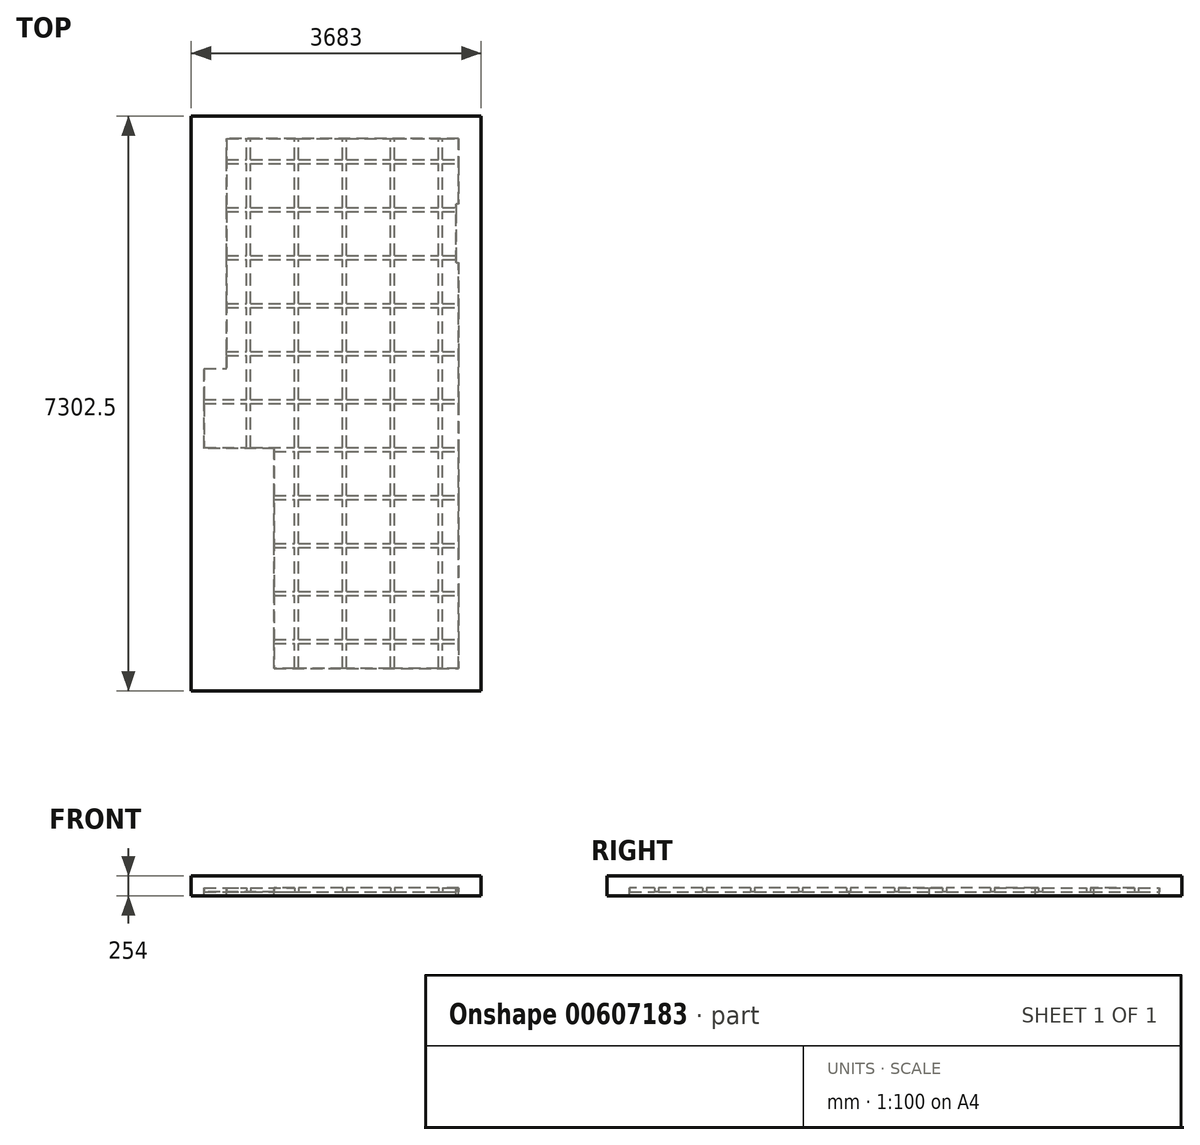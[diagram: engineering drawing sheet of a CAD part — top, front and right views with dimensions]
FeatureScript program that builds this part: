
annotation { "Feature Type Name" : "Feature", "Feature Type Description" : "" }
export const myFeature = defineFeature(function(context is Context, id is Id, definition is map)
    precondition{}
    {
        {
            var Q0;
            Q0=qCreatedBy(makeId("Top.planeOp"),FACE);
            var sketch = newSketch(context, id + "F0", { "sketchPlane" : qUnion([Q0])});
            skLineSegment(sketch, "E0", {"start": v(0, 0) * mm, "end": v(0, 5156.2) * mm});
            skLineSegment(sketch, "E1", {"start": v(0, 5156.2) * mm, "end": v(-34.92, 5156.2) * mm});
            skLineSegment(sketch, "E2", {"start": v(-34.92, 5156.2) * mm, "end": v(-34.92, 5899.15) * mm});
            skLineSegment(sketch, "E3", {"start": v(-34.92, 5899.15) * mm, "end": v(0, 5899.15) * mm});
            skLineSegment(sketch, "E4", {"start": v(0, 5899.15) * mm, "end": v(0, 6731) * mm});
            skLineSegment(sketch, "E5", {"start": v(0, 6731) * mm, "end": v(-2946.4, 6731) * mm});
            skLineSegment(sketch, "E6", {"start": v(-2946.4, 6731) * mm, "end": v(-2946.4, 3810) * mm});
            skLineSegment(sketch, "E7", {"start": v(-2946.4, 3810) * mm, "end": v(-3232.15, 3810) * mm});
            skLineSegment(sketch, "E8", {"start": v(-3232.15, 3810) * mm, "end": v(-3232.15, 2794) * mm});
            skLineSegment(sketch, "E9", {"start": v(-3232.15, 2794) * mm, "end": v(-2343.15, 2794) * mm});
            skLineSegment(sketch, "E10", {"start": v(-2343.15, 2794) * mm, "end": v(-2343.15, 0) * mm});
            skLineSegment(sketch, "E11", {"start": v(-2343.15, 0) * mm, "end": v(0, 0) * mm});
            skLineSegment(sketch, "E12", {"start": v(285.75, 7016.75) * mm, "end": v(285.75, -285.75) * mm});
            skLineSegment(sketch, "E13", {"start": v(285.75, -285.75) * mm, "end": v(-3397.25, -285.75) * mm});
            skLineSegment(sketch, "E14", {"start": v(285.75, 7016.75) * mm, "end": v(-3397.25, 7016.75) * mm});
            skLineSegment(sketch, "E15", {"start": v(-3397.25, 7016.75) * mm, "end": v(-3397.25, -285.75) * mm});
            skSolve(sketch);
        }
        {
            var Q0;
            Q0=makeQuery(id+"F0.imprint","IMPRINT",FACE,{"disambiguationData":[TD([[makeQuery(id+"F0.imprint","IMPRINT",EDGE,{"derivedFrom":sQuery(id+"F0.wireOp",EDGE,"E0")}),-1.0]])]});
            extrude(context, id + "F1", {"entities" : qUnion([Q0]), "oppositeDirection" : true, "depth" : 254 * mm, "offsetDistance" : 25.4 * mm});
        }
        {
            var Q0;
            Q0=qSketchRegion(id+"F0",true);
            var Q1;
            Q1=makeQuery(id+"F0.imprint","IMPRINT",FACE,{"disambiguationData":[TD([[makeQuery(id+"F0.imprint","IMPRINT",EDGE,{"derivedFrom":sQuery(id+"F0.wireOp",EDGE,"E0")}),1.0]])]});
            extrude(context, id + "F2", {"entities" : qUnion([Q0, Q1]), "operationType" : NewBodyOperationType.ADD, "oppositeDirection" : true, "depth" : 203.2 * mm, "offsetDistance" : 25.4 * mm});
        }
        {
            var Q0;
            Q0=makeQuery(id+"F2.opExtrude","CAP_FACE",FACE,{"disambiguationData":[OSD([sQuery(id+"F0.wireOp",EDGE,"E12"),sQuery(id+"F0.wireOp",EDGE,"E13"),sQuery(id+"F0.wireOp",EDGE,"E14"),sQuery(id+"F0.wireOp",EDGE,"E15")])],"isStart":false});
            var sketch = newSketch(context, id + "F3", { "sketchPlane" : qUnion([Q0])});
            skLineSegment(sketch, "E16.bottom", {"start": v(-2035.18, 0) * mm, "end": v(-2085.98, 0) * mm});
            skLineSegment(sketch, "E16.top", {"start": v(-2035.18, -6731) * mm, "end": v(-2085.98, -6731) * mm});
            skLineSegment(sketch, "E16.left", {"start": v(-2035.18, 0) * mm, "end": v(-2035.18, -317.5) * mm});
            skLineSegment(sketch, "E16.right", {"start": v(-2085.98, 0) * mm, "end": v(-2085.98, -317.5) * mm});
            skLineSegment(sketch, "E17.bottom", {"start": v(-1425.58, 0) * mm, "end": v(-1476.38, 0) * mm});
            skLineSegment(sketch, "E17.top", {"start": v(-1425.58, -6731) * mm, "end": v(-1476.38, -6731) * mm});
            skLineSegment(sketch, "E17.left", {"start": v(-1425.58, 0) * mm, "end": v(-1425.58, -317.5) * mm});
            skLineSegment(sketch, "E17.right", {"start": v(-1476.38, 0) * mm, "end": v(-1476.38, -317.5) * mm});
            skPoint(sketch, "E18.oppositeSnap0", {"position": v(-866.78, 0) * mm});
            skLineSegment(sketch, "E18.bottom", {"start": v(-815.98, 0) * mm, "end": v(-866.78, 0) * mm});
            skLineSegment(sketch, "E18.top", {"start": v(-815.98, -6731) * mm, "end": v(-866.78, -6731) * mm});
            skLineSegment(sketch, "E18.left", {"start": v(-815.98, 0) * mm, "end": v(-815.98, -317.5) * mm});
            skLineSegment(sketch, "E18.right", {"start": v(-866.78, 0) * mm, "end": v(-866.78, -317.5) * mm});
            skLineSegment(sketch, "E19.bottom", {"start": v(-257.18, 0) * mm, "end": v(-206.38, 0) * mm});
            skLineSegment(sketch, "E19.top", {"start": v(-257.18, -6731) * mm, "end": v(-206.38, -6731) * mm});
            skLineSegment(sketch, "E19.left", {"start": v(-257.18, 0) * mm, "end": v(-257.18, -317.5) * mm});
            skLineSegment(sketch, "E19.right", {"start": v(-206.38, 0) * mm, "end": v(-206.38, -317.5) * mm});
            skLineSegment(sketch, "E20.bottom", {"start": v(-2695.58, -2794) * mm, "end": v(-2644.78, -2794) * mm});
            skLineSegment(sketch, "E20.top", {"start": v(-2695.58, -6731) * mm, "end": v(-2644.78, -6731) * mm});
            skLineSegment(sketch, "E20.left", {"start": v(-2695.58, -2794) * mm, "end": v(-2695.58, -3365.5) * mm});
            skLineSegment(sketch, "E20.right", {"start": v(-2644.78, -2794) * mm, "end": v(-2644.78, -3365.5) * mm});
            skLineSegment(sketch, "E21.bottom", {"start": v(-2946.4, -6413.5) * mm, "end": v(-2695.58, -6413.5) * mm});
            skLineSegment(sketch, "E21.top", {"start": v(-2946.4, -6464.3) * mm, "end": v(-2695.58, -6464.3) * mm});
            skLineSegment(sketch, "E21.left", {"start": v(-2946.4, -6413.5) * mm, "end": v(-2946.4, -6464.3) * mm});
            skLineSegment(sketch, "E21.right", {"start": v(0, -6413.5) * mm, "end": v(0, -6464.3) * mm});
            skLineSegment(sketch, "E22.bottom", {"start": v(-2946.4, -5854.7) * mm, "end": v(-2695.58, -5854.7) * mm});
            skLineSegment(sketch, "E22.top", {"start": v(-2946.4, -5803.9) * mm, "end": v(-2695.58, -5803.9) * mm});
            skLineSegment(sketch, "E22.left", {"start": v(-2946.4, -5854.7) * mm, "end": v(-2946.4, -5803.9) * mm});
            skLineSegment(sketch, "E22.right", {"start": v(-34.92, -5854.7) * mm, "end": v(-34.92, -5803.9) * mm});
            skLineSegment(sketch, "E23.bottom", {"start": v(-2946.4, -5245.1) * mm, "end": v(-2695.58, -5245.1) * mm});
            skLineSegment(sketch, "E23.top", {"start": v(-2946.4, -5194.3) * mm, "end": v(-2695.58, -5194.3) * mm});
            skLineSegment(sketch, "E23.left", {"start": v(-2946.4, -5245.1) * mm, "end": v(-2946.4, -5194.3) * mm});
            skLineSegment(sketch, "E23.right", {"start": v(0, -5245.1) * mm, "end": v(0, -5194.3) * mm});
            skLineSegment(sketch, "E24.bottom", {"start": v(-2946.4, -4584.7) * mm, "end": v(-2695.58, -4584.7) * mm});
            skLineSegment(sketch, "E24.top", {"start": v(-2946.4, -4635.5) * mm, "end": v(-2695.58, -4635.5) * mm});
            skLineSegment(sketch, "E24.left", {"start": v(-2946.4, -4584.7) * mm, "end": v(-2946.4, -4635.5) * mm});
            skLineSegment(sketch, "E24.right", {"start": v(0, -4584.7) * mm, "end": v(0, -4635.5) * mm});
            skLineSegment(sketch, "E25.bottom", {"start": v(-2946.4, -3975.1) * mm, "end": v(-2695.58, -3975.1) * mm});
            skLineSegment(sketch, "E25.top", {"start": v(-2946.4, -4025.9) * mm, "end": v(-2695.58, -4025.9) * mm});
            skLineSegment(sketch, "E25.left", {"start": v(-2946.4, -3975.1) * mm, "end": v(-2946.4, -4025.9) * mm});
            skLineSegment(sketch, "E25.right", {"start": v(0, -3975.1) * mm, "end": v(0, -4025.9) * mm});
            skLineSegment(sketch, "E26.bottom", {"start": v(-3232.15, -3365.5) * mm, "end": v(-2695.58, -3365.5) * mm});
            skLineSegment(sketch, "E26.top", {"start": v(-3232.15, -3416.3) * mm, "end": v(-2695.58, -3416.3) * mm});
            skLineSegment(sketch, "E26.left", {"start": v(-3232.15, -3365.5) * mm, "end": v(-3232.15, -3416.3) * mm});
            skLineSegment(sketch, "E26.right", {"start": v(0, -3365.5) * mm, "end": v(0, -3416.3) * mm});
            skLineSegment(sketch, "E27.bottom", {"start": v(-3232.15, -2755.9) * mm, "end": v(-2085.98, -2755.9) * mm});
            skLineSegment(sketch, "E27.top", {"start": v(-3232.15, -2806.7) * mm, "end": v(-2695.58, -2806.7) * mm});
            skLineSegment(sketch, "E27.left", {"start": v(-3232.15, -2755.9) * mm, "end": v(-3232.15, -2806.7) * mm});
            skLineSegment(sketch, "E27.right", {"start": v(0, -2755.9) * mm, "end": v(0, -2806.7) * mm});
            skLineSegment(sketch, "E28.bottom", {"start": v(-2343.15, -2146.3) * mm, "end": v(-2085.98, -2146.3) * mm});
            skLineSegment(sketch, "E28.top", {"start": v(-2343.15, -2197.1) * mm, "end": v(-2085.98, -2197.1) * mm});
            skLineSegment(sketch, "E28.left", {"start": v(-2343.15, -2146.3) * mm, "end": v(-2343.15, -2197.1) * mm});
            skLineSegment(sketch, "E28.right", {"start": v(0, -2146.3) * mm, "end": v(0, -2197.1) * mm});
            skLineSegment(sketch, "E29.bottom", {"start": v(-2343.15, -1536.7) * mm, "end": v(-2085.98, -1536.7) * mm});
            skLineSegment(sketch, "E29.top", {"start": v(-2343.15, -1587.5) * mm, "end": v(-2085.98, -1587.5) * mm});
            skLineSegment(sketch, "E29.left", {"start": v(-2343.15, -1536.7) * mm, "end": v(-2343.15, -1587.5) * mm});
            skLineSegment(sketch, "E29.right", {"start": v(0, -1536.7) * mm, "end": v(0, -1587.5) * mm});
            skLineSegment(sketch, "E30.bottom", {"start": v(-2343.15, -927.1) * mm, "end": v(-2085.98, -927.1) * mm});
            skLineSegment(sketch, "E30.top", {"start": v(-2343.15, -977.9) * mm, "end": v(-2085.98, -977.9) * mm});
            skLineSegment(sketch, "E30.left", {"start": v(-2343.15, -927.1) * mm, "end": v(-2343.15, -977.9) * mm});
            skLineSegment(sketch, "E30.right", {"start": v(0, -927.1) * mm, "end": v(0, -977.9) * mm});
            skLineSegment(sketch, "E31.bottom", {"start": v(-2343.15, -317.5) * mm, "end": v(-2085.98, -317.5) * mm});
            skLineSegment(sketch, "E31.top", {"start": v(-2343.15, -368.3) * mm, "end": v(-2085.98, -368.3) * mm});
            skLineSegment(sketch, "E31.left", {"start": v(-2343.15, -317.5) * mm, "end": v(-2343.15, -368.3) * mm});
            skLineSegment(sketch, "E31.right", {"start": v(0, -317.5) * mm, "end": v(0, -368.3) * mm});
            skLineSegment(sketch, "E32.trimOffspring", {"start": v(-2085.98, -2806.7) * mm, "end": v(-2085.98, -3365.5) * mm});
            skLineSegment(sketch, "E33.trimOffspring", {"start": v(-2035.18, -2806.7) * mm, "end": v(-2035.18, -3365.5) * mm});
            skLineSegment(sketch, "E34.trimOffspring", {"start": v(-2035.18, -2755.9) * mm, "end": v(-1476.38, -2755.9) * mm});
            skLineSegment(sketch, "E35.trimOffspring", {"start": v(-1476.38, -2806.7) * mm, "end": v(-1476.38, -3365.5) * mm});
            skLineSegment(sketch, "E36.trimOffspring", {"start": v(-1425.58, -2755.9) * mm, "end": v(0, -2755.9) * mm});
            skLineSegment(sketch, "E37.trimOffspring", {"start": v(-1425.58, -2806.7) * mm, "end": v(-1425.58, -3365.5) * mm});
            skLineSegment(sketch, "E38.trimOffspring", {"start": v(-1425.58, -2806.7) * mm, "end": v(0, -2806.7) * mm});
            skLineSegment(sketch, "E39.trimOffspring", {"start": v(-2035.18, -317.5) * mm, "end": v(-1476.38, -317.5) * mm});
            skLineSegment(sketch, "E40.trimOffspring", {"start": v(-2085.98, -368.3) * mm, "end": v(-2085.98, -927.1) * mm});
            skLineSegment(sketch, "E41.trimOffspring", {"start": v(-2035.18, -368.3) * mm, "end": v(-2035.18, -927.1) * mm});
            skLineSegment(sketch, "E42.trimOffspring", {"start": v(-2035.18, -368.3) * mm, "end": v(-1476.38, -368.3) * mm});
            skLineSegment(sketch, "E43.trimOffspring", {"start": v(-1476.38, -368.3) * mm, "end": v(-1476.38, -927.1) * mm});
            skLineSegment(sketch, "E44.trimOffspring", {"start": v(-1425.58, -317.5) * mm, "end": v(-866.78, -317.5) * mm});
            skLineSegment(sketch, "E45.trimOffspring", {"start": v(-1425.58, -368.3) * mm, "end": v(-1425.58, -927.1) * mm});
            skLineSegment(sketch, "E46.trimOffspring", {"start": v(-1425.58, -368.3) * mm, "end": v(-866.78, -368.3) * mm});
            skLineSegment(sketch, "E47.trimOffspring", {"start": v(-866.78, -368.3) * mm, "end": v(-866.78, -927.1) * mm});
            skLineSegment(sketch, "E48.trimOffspring", {"start": v(-815.98, -317.5) * mm, "end": v(-257.18, -317.5) * mm});
            skLineSegment(sketch, "E49.trimOffspring", {"start": v(-815.98, -368.3) * mm, "end": v(-257.18, -368.3) * mm});
            skLineSegment(sketch, "E50.trimOffspring", {"start": v(-815.98, -368.3) * mm, "end": v(-815.98, -927.1) * mm});
            skLineSegment(sketch, "E51.trimOffspring", {"start": v(-257.18, -368.3) * mm, "end": v(-257.18, -927.1) * mm});
            skLineSegment(sketch, "E52.trimOffspring", {"start": v(-206.37, -317.5) * mm, "end": v(0, -317.5) * mm});
            skLineSegment(sketch, "E53.trimOffspring", {"start": v(-206.38, -368.3) * mm, "end": v(-206.38, -927.1) * mm});
            skLineSegment(sketch, "E54.trimOffspring", {"start": v(-206.37, -368.3) * mm, "end": v(0, -368.3) * mm});
            skLineSegment(sketch, "E55.trimOffspring", {"start": v(-206.37, -927.1) * mm, "end": v(0, -927.1) * mm});
            skLineSegment(sketch, "E56.trimOffspring", {"start": v(-206.37, -977.9) * mm, "end": v(0, -977.9) * mm});
            skLineSegment(sketch, "E57.trimOffspring", {"start": v(-206.38, -977.9) * mm, "end": v(-206.38, -1536.7) * mm});
            skLineSegment(sketch, "E58.trimOffspring", {"start": v(-257.18, -977.9) * mm, "end": v(-257.18, -1536.7) * mm});
            skLineSegment(sketch, "E59.trimOffspring", {"start": v(-815.98, -977.9) * mm, "end": v(-815.98, -1536.7) * mm});
            skLineSegment(sketch, "E60.trimOffspring", {"start": v(-866.78, -977.9) * mm, "end": v(-866.78, -1536.7) * mm});
            skLineSegment(sketch, "E61.trimOffspring", {"start": v(-815.98, -927.1) * mm, "end": v(-257.18, -927.1) * mm});
            skLineSegment(sketch, "E62.trimOffspring", {"start": v(-815.98, -977.9) * mm, "end": v(-257.18, -977.9) * mm});
            skLineSegment(sketch, "E63.trimOffspring", {"start": v(-1425.58, -977.9) * mm, "end": v(-1425.58, -1536.7) * mm});
            skLineSegment(sketch, "E64.trimOffspring", {"start": v(-1425.58, -927.1) * mm, "end": v(-866.78, -927.1) * mm});
            skLineSegment(sketch, "E65.trimOffspring", {"start": v(-1425.58, -977.9) * mm, "end": v(-866.78, -977.9) * mm});
            skLineSegment(sketch, "E66.trimOffspring", {"start": v(-1476.38, -977.9) * mm, "end": v(-1476.38, -1536.7) * mm});
            skLineSegment(sketch, "E67.trimOffspring", {"start": v(-2035.18, -977.9) * mm, "end": v(-2035.18, -1536.7) * mm});
            skLineSegment(sketch, "E68.trimOffspring", {"start": v(-2035.18, -927.1) * mm, "end": v(-1476.38, -927.1) * mm});
            skLineSegment(sketch, "E69.trimOffspring", {"start": v(-2085.98, -977.9) * mm, "end": v(-2085.98, -1536.7) * mm});
            skLineSegment(sketch, "E70.trimOffspring", {"start": v(-2035.18, -977.9) * mm, "end": v(-1476.38, -977.9) * mm});
            skLineSegment(sketch, "E71.trimOffspring", {"start": v(-2035.18, -1536.7) * mm, "end": v(-1476.38, -1536.7) * mm});
            skLineSegment(sketch, "E72.trimOffspring", {"start": v(-2085.98, -1587.5) * mm, "end": v(-2085.98, -2146.3) * mm});
            skLineSegment(sketch, "E73.trimOffspring", {"start": v(-2035.18, -1587.5) * mm, "end": v(-2035.18, -2146.3) * mm});
            skLineSegment(sketch, "E74.trimOffspring", {"start": v(-2035.18, -1587.5) * mm, "end": v(-1476.38, -1587.5) * mm});
            skLineSegment(sketch, "E75.trimOffspring", {"start": v(-1476.38, -1587.5) * mm, "end": v(-1476.38, -2146.3) * mm});
            skLineSegment(sketch, "E76.trimOffspring", {"start": v(-1425.58, -1536.7) * mm, "end": v(-866.78, -1536.7) * mm});
            skLineSegment(sketch, "E77.trimOffspring", {"start": v(-1425.58, -1587.5) * mm, "end": v(-1425.58, -2146.3) * mm});
            skLineSegment(sketch, "E78.trimOffspring", {"start": v(-1425.58, -1587.5) * mm, "end": v(-866.78, -1587.5) * mm});
            skLineSegment(sketch, "E79.trimOffspring", {"start": v(-866.78, -1587.5) * mm, "end": v(-866.78, -2146.3) * mm});
            skLineSegment(sketch, "E80.trimOffspring", {"start": v(-815.98, -1536.7) * mm, "end": v(-257.18, -1536.7) * mm});
            skLineSegment(sketch, "E81.trimOffspring", {"start": v(-815.98, -1587.5) * mm, "end": v(-815.98, -2146.3) * mm});
            skLineSegment(sketch, "E82.trimOffspring", {"start": v(-815.98, -1587.5) * mm, "end": v(-257.18, -1587.5) * mm});
            skLineSegment(sketch, "E83.trimOffspring", {"start": v(-257.18, -1587.5) * mm, "end": v(-257.18, -2146.3) * mm});
            skLineSegment(sketch, "E84.trimOffspring", {"start": v(-206.37, -1536.7) * mm, "end": v(0, -1536.7) * mm});
            skLineSegment(sketch, "E85.trimOffspring", {"start": v(-206.38, -1587.5) * mm, "end": v(-206.38, -2146.3) * mm});
            skLineSegment(sketch, "E86.trimOffspring", {"start": v(-206.37, -1587.5) * mm, "end": v(0, -1587.5) * mm});
            skLineSegment(sketch, "E87.trimOffspring", {"start": v(-206.37, -2146.3) * mm, "end": v(0, -2146.3) * mm});
            skLineSegment(sketch, "E88.trimOffspring", {"start": v(-257.18, -2197.1) * mm, "end": v(-257.18, -3365.5) * mm});
            skLineSegment(sketch, "E89.trimOffspring", {"start": v(-206.37, -2197.1) * mm, "end": v(0, -2197.1) * mm});
            skLineSegment(sketch, "E90.trimOffspring", {"start": v(-206.38, -2197.1) * mm, "end": v(-206.38, -3365.5) * mm});
            skLineSegment(sketch, "E91.trimOffspring", {"start": v(-815.98, -2197.1) * mm, "end": v(-815.98, -3365.5) * mm});
            skLineSegment(sketch, "E92.trimOffspring", {"start": v(-815.98, -2146.3) * mm, "end": v(-257.18, -2146.3) * mm});
            skLineSegment(sketch, "E93.trimOffspring", {"start": v(-866.78, -2197.1) * mm, "end": v(-866.78, -3365.5) * mm});
            skLineSegment(sketch, "E94.trimOffspring", {"start": v(-815.98, -2197.1) * mm, "end": v(-257.18, -2197.1) * mm});
            skLineSegment(sketch, "E95.trimOffspring", {"start": v(-1425.58, -2197.1) * mm, "end": v(-1425.58, -2755.9) * mm});
            skLineSegment(sketch, "E96.trimOffspring", {"start": v(-1425.58, -2146.3) * mm, "end": v(-866.78, -2146.3) * mm});
            skLineSegment(sketch, "E97.trimOffspring", {"start": v(-1476.38, -2197.1) * mm, "end": v(-1476.38, -2755.9) * mm});
            skLineSegment(sketch, "E98.trimOffspring", {"start": v(-1425.58, -2197.1) * mm, "end": v(-866.78, -2197.1) * mm});
            skLineSegment(sketch, "E99.trimOffspring", {"start": v(-2035.18, -2197.1) * mm, "end": v(-2035.18, -2755.9) * mm});
            skLineSegment(sketch, "E100.trimOffspring", {"start": v(-2035.18, -2146.3) * mm, "end": v(-1476.38, -2146.3) * mm});
            skLineSegment(sketch, "E101.trimOffspring", {"start": v(-2085.98, -2197.1) * mm, "end": v(-2085.98, -2755.9) * mm});
            skLineSegment(sketch, "E102.trimOffspring", {"start": v(-2035.18, -2197.1) * mm, "end": v(-1476.38, -2197.1) * mm});
            skLineSegment(sketch, "E103.trimOffspring", {"start": v(-2644.78, -2806.7) * mm, "end": v(-1476.38, -2806.7) * mm});
            skLineSegment(sketch, "E104.trimOffspring", {"start": v(-2644.78, -3365.5) * mm, "end": v(-2085.98, -3365.5) * mm});
            skLineSegment(sketch, "E105.trimOffspring", {"start": v(-2695.58, -3416.3) * mm, "end": v(-2695.58, -3975.1) * mm});
            skLineSegment(sketch, "E106.trimOffspring", {"start": v(-2644.78, -3416.3) * mm, "end": v(-2644.78, -3975.1) * mm});
            skLineSegment(sketch, "E107.trimOffspring", {"start": v(-2644.78, -3416.3) * mm, "end": v(-2085.98, -3416.3) * mm});
            skLineSegment(sketch, "E108.trimOffspring", {"start": v(-2085.98, -3416.3) * mm, "end": v(-2085.98, -3975.1) * mm});
            skLineSegment(sketch, "E109.trimOffspring", {"start": v(-2035.18, -3365.5) * mm, "end": v(-1476.38, -3365.5) * mm});
            skLineSegment(sketch, "E110.trimOffspring", {"start": v(-2035.18, -3416.3) * mm, "end": v(-2035.18, -3975.1) * mm});
            skLineSegment(sketch, "E111.trimOffspring", {"start": v(-2035.18, -3416.3) * mm, "end": v(-1476.38, -3416.3) * mm});
            skLineSegment(sketch, "E112.trimOffspring", {"start": v(-1476.38, -3416.3) * mm, "end": v(-1476.38, -3975.1) * mm});
            skLineSegment(sketch, "E113.trimOffspring", {"start": v(-1425.58, -3365.5) * mm, "end": v(-866.78, -3365.5) * mm});
            skLineSegment(sketch, "E114.trimOffspring", {"start": v(-1425.58, -3416.3) * mm, "end": v(-1425.58, -3975.1) * mm});
            skLineSegment(sketch, "E115.trimOffspring", {"start": v(-1425.58, -3416.3) * mm, "end": v(-866.78, -3416.3) * mm});
            skLineSegment(sketch, "E116.trimOffspring", {"start": v(-206.38, -3416.3) * mm, "end": v(-206.38, -3975.1) * mm});
            skLineSegment(sketch, "E117.trimOffspring", {"start": v(-206.37, -3365.5) * mm, "end": v(0, -3365.5) * mm});
            skLineSegment(sketch, "E118.trimOffspring", {"start": v(-257.18, -3416.3) * mm, "end": v(-257.18, -3975.1) * mm});
            skLineSegment(sketch, "E119.trimOffspring", {"start": v(-206.37, -3416.3) * mm, "end": v(0, -3416.3) * mm});
            skLineSegment(sketch, "E120.trimOffspring", {"start": v(-815.98, -3416.3) * mm, "end": v(-815.98, -3975.1) * mm});
            skLineSegment(sketch, "E121.trimOffspring", {"start": v(-815.98, -3365.5) * mm, "end": v(-257.18, -3365.5) * mm});
            skLineSegment(sketch, "E122.trimOffspring", {"start": v(-866.78, -3416.3) * mm, "end": v(-866.78, -3975.1) * mm});
            skLineSegment(sketch, "E123.trimOffspring", {"start": v(-815.98, -3416.3) * mm, "end": v(-257.18, -3416.3) * mm});
            skLineSegment(sketch, "E124.trimOffspring", {"start": v(-206.38, -4025.9) * mm, "end": v(-206.38, -4584.7) * mm});
            skLineSegment(sketch, "E125.trimOffspring", {"start": v(-206.37, -3975.1) * mm, "end": v(0, -3975.1) * mm});
            skLineSegment(sketch, "E126.trimOffspring", {"start": v(-206.37, -4025.9) * mm, "end": v(0, -4025.9) * mm});
            skLineSegment(sketch, "E127.trimOffspring", {"start": v(-257.18, -4025.9) * mm, "end": v(-257.18, -4584.7) * mm});
            skLineSegment(sketch, "E128.trimOffspring", {"start": v(-815.98, -4025.9) * mm, "end": v(-815.98, -4584.7) * mm});
            skLineSegment(sketch, "E129.trimOffspring", {"start": v(-815.98, -3975.1) * mm, "end": v(-257.18, -3975.1) * mm});
            skLineSegment(sketch, "E130.trimOffspring", {"start": v(-866.78, -4025.9) * mm, "end": v(-866.78, -4584.7) * mm});
            skLineSegment(sketch, "E131.trimOffspring", {"start": v(-815.98, -4025.9) * mm, "end": v(-257.18, -4025.9) * mm});
            skLineSegment(sketch, "E132.trimOffspring", {"start": v(-1425.58, -4025.9) * mm, "end": v(-1425.58, -4584.7) * mm});
            skLineSegment(sketch, "E133.trimOffspring", {"start": v(-1425.58, -3975.1) * mm, "end": v(-866.78, -3975.1) * mm});
            skLineSegment(sketch, "E134.trimOffspring", {"start": v(-1476.38, -4025.9) * mm, "end": v(-1476.38, -4584.7) * mm});
            skLineSegment(sketch, "E135.trimOffspring", {"start": v(-1425.58, -4025.9) * mm, "end": v(-866.78, -4025.9) * mm});
            skLineSegment(sketch, "E136.trimOffspring", {"start": v(-2035.18, -3975.1) * mm, "end": v(-1476.38, -3975.1) * mm});
            skLineSegment(sketch, "E137.trimOffspring", {"start": v(-2035.18, -4025.9) * mm, "end": v(-2035.18, -4584.7) * mm});
            skLineSegment(sketch, "E138.trimOffspring", {"start": v(-2035.18, -4025.9) * mm, "end": v(-1476.38, -4025.9) * mm});
            skLineSegment(sketch, "E139.trimOffspring", {"start": v(-2085.98, -4025.9) * mm, "end": v(-2085.98, -4584.7) * mm});
            skLineSegment(sketch, "E140.trimOffspring", {"start": v(-2644.78, -4025.9) * mm, "end": v(-2644.78, -4584.7) * mm});
            skLineSegment(sketch, "E141.trimOffspring", {"start": v(-2644.78, -3975.1) * mm, "end": v(-2085.98, -3975.1) * mm});
            skLineSegment(sketch, "E142.trimOffspring", {"start": v(-2695.58, -4025.9) * mm, "end": v(-2695.58, -4584.7) * mm});
            skLineSegment(sketch, "E143.trimOffspring", {"start": v(-2644.78, -4025.9) * mm, "end": v(-2085.98, -4025.9) * mm});
            skLineSegment(sketch, "E144.trimOffspring", {"start": v(-2644.78, -4584.7) * mm, "end": v(-2085.98, -4584.7) * mm});
            skLineSegment(sketch, "E145.trimOffspring", {"start": v(-2695.58, -4635.5) * mm, "end": v(-2695.58, -5194.3) * mm});
            skLineSegment(sketch, "E146.trimOffspring", {"start": v(-2644.78, -4635.5) * mm, "end": v(-2644.78, -5194.3) * mm});
            skLineSegment(sketch, "E147.trimOffspring", {"start": v(-2644.78, -4635.5) * mm, "end": v(-2085.98, -4635.5) * mm});
            skLineSegment(sketch, "E148.trimOffspring", {"start": v(-2035.18, -4584.7) * mm, "end": v(-1476.38, -4584.7) * mm});
            skLineSegment(sketch, "E149.trimOffspring", {"start": v(-2085.98, -4635.5) * mm, "end": v(-2085.98, -5194.3) * mm});
            skLineSegment(sketch, "E150.trimOffspring", {"start": v(-2035.18, -4635.5) * mm, "end": v(-2035.18, -5194.3) * mm});
            skLineSegment(sketch, "E151.trimOffspring", {"start": v(-2035.18, -4635.5) * mm, "end": v(-1476.38, -4635.5) * mm});
            skLineSegment(sketch, "E152.trimOffspring", {"start": v(-1425.58, -4584.7) * mm, "end": v(-866.78, -4584.7) * mm});
            skLineSegment(sketch, "E153.trimOffspring", {"start": v(-1476.38, -4635.5) * mm, "end": v(-1476.38, -5194.3) * mm});
            skLineSegment(sketch, "E154.trimOffspring", {"start": v(-1425.58, -4635.5) * mm, "end": v(-1425.58, -5194.3) * mm});
            skLineSegment(sketch, "E155.trimOffspring", {"start": v(-1425.58, -4635.5) * mm, "end": v(-866.78, -4635.5) * mm});
            skLineSegment(sketch, "E156.trimOffspring", {"start": v(-815.98, -4584.7) * mm, "end": v(-257.18, -4584.7) * mm});
            skLineSegment(sketch, "E157.trimOffspring", {"start": v(-866.78, -4635.5) * mm, "end": v(-866.78, -5194.3) * mm});
            skLineSegment(sketch, "E158.trimOffspring", {"start": v(-815.98, -4635.5) * mm, "end": v(-257.18, -4635.5) * mm});
            skLineSegment(sketch, "E159.trimOffspring", {"start": v(-815.98, -4635.5) * mm, "end": v(-815.98, -5194.3) * mm});
            skLineSegment(sketch, "E160.trimOffspring", {"start": v(-206.37, -4584.7) * mm, "end": v(0, -4584.7) * mm});
            skLineSegment(sketch, "E161.trimOffspring", {"start": v(-257.18, -4635.5) * mm, "end": v(-257.18, -5194.3) * mm});
            skLineSegment(sketch, "E162.trimOffspring", {"start": v(-206.38, -4635.5) * mm, "end": v(-206.38, -5194.3) * mm});
            skLineSegment(sketch, "E163.trimOffspring", {"start": v(-206.37, -4635.5) * mm, "end": v(0, -4635.5) * mm});
            skLineSegment(sketch, "E164.trimOffspring", {"start": v(-2644.78, -5194.3) * mm, "end": v(-2085.98, -5194.3) * mm});
            skLineSegment(sketch, "E165.trimOffspring", {"start": v(-2695.58, -5245.1) * mm, "end": v(-2695.58, -5803.9) * mm});
            skLineSegment(sketch, "E166.trimOffspring", {"start": v(-2644.78, -5245.1) * mm, "end": v(-2085.98, -5245.1) * mm});
            skLineSegment(sketch, "E167.trimOffspring", {"start": v(-2644.78, -5245.1) * mm, "end": v(-2644.78, -5803.9) * mm});
            skLineSegment(sketch, "E168.trimOffspring", {"start": v(-2644.78, -5803.9) * mm, "end": v(-2085.98, -5803.9) * mm});
            skLineSegment(sketch, "E169.trimOffspring", {"start": v(-2695.58, -5854.7) * mm, "end": v(-2695.58, -6413.5) * mm});
            skLineSegment(sketch, "E170.trimOffspring", {"start": v(-2644.78, -5854.7) * mm, "end": v(-2085.98, -5854.7) * mm});
            skLineSegment(sketch, "E171.trimOffspring", {"start": v(-2644.78, -5854.7) * mm, "end": v(-2644.78, -6413.5) * mm});
            skLineSegment(sketch, "E172.trimOffspring", {"start": v(-2644.78, -6413.5) * mm, "end": v(-2085.98, -6413.5) * mm});
            skLineSegment(sketch, "E173.trimOffspring", {"start": v(-2695.58, -6464.3) * mm, "end": v(-2695.58, -6731) * mm});
            skLineSegment(sketch, "E174.trimOffspring", {"start": v(-2644.78, -6464.3) * mm, "end": v(-2085.98, -6464.3) * mm});
            skLineSegment(sketch, "E175.trimOffspring", {"start": v(-2644.78, -6464.3) * mm, "end": v(-2644.78, -6731) * mm});
            skLineSegment(sketch, "E176.trimOffspring", {"start": v(-2085.98, -5245.1) * mm, "end": v(-2085.98, -5803.9) * mm});
            skLineSegment(sketch, "E177.trimOffspring", {"start": v(-2035.18, -5194.3) * mm, "end": v(-1476.38, -5194.3) * mm});
            skLineSegment(sketch, "E178.trimOffspring", {"start": v(-2035.18, -5245.1) * mm, "end": v(-2035.18, -5803.9) * mm});
            skLineSegment(sketch, "E179.trimOffspring", {"start": v(-2035.18, -5245.1) * mm, "end": v(-1476.38, -5245.1) * mm});
            skLineSegment(sketch, "E180.trimOffspring", {"start": v(-2035.18, -5803.9) * mm, "end": v(-1476.38, -5803.9) * mm});
            skLineSegment(sketch, "E181.trimOffspring", {"start": v(-2085.98, -5854.7) * mm, "end": v(-2085.98, -6413.5) * mm});
            skLineSegment(sketch, "E182.trimOffspring", {"start": v(-2035.18, -5854.7) * mm, "end": v(-2035.18, -6413.5) * mm});
            skLineSegment(sketch, "E183.trimOffspring", {"start": v(-2035.18, -5854.7) * mm, "end": v(-1476.38, -5854.7) * mm});
            skLineSegment(sketch, "E184.trimOffspring", {"start": v(-2035.18, -6413.5) * mm, "end": v(-1476.38, -6413.5) * mm});
            skLineSegment(sketch, "E185.trimOffspring", {"start": v(-2085.98, -6464.3) * mm, "end": v(-2085.98, -6731) * mm});
            skLineSegment(sketch, "E186.trimOffspring", {"start": v(-2035.18, -6464.3) * mm, "end": v(-1476.38, -6464.3) * mm});
            skLineSegment(sketch, "E187.trimOffspring", {"start": v(-2035.18, -6464.3) * mm, "end": v(-2035.18, -6731) * mm});
            skLineSegment(sketch, "E188.trimOffspring", {"start": v(-1425.58, -5194.3) * mm, "end": v(-866.78, -5194.3) * mm});
            skLineSegment(sketch, "E189.trimOffspring", {"start": v(-1476.38, -5245.1) * mm, "end": v(-1476.38, -5803.9) * mm});
            skLineSegment(sketch, "E190.trimOffspring", {"start": v(-1425.58, -5245.1) * mm, "end": v(-1425.58, -5803.9) * mm});
            skLineSegment(sketch, "E191.trimOffspring", {"start": v(-1425.58, -5245.1) * mm, "end": v(-866.78, -5245.1) * mm});
            skLineSegment(sketch, "E192.trimOffspring", {"start": v(-1425.58, -5803.9) * mm, "end": v(-866.78, -5803.9) * mm});
            skLineSegment(sketch, "E193.trimOffspring", {"start": v(-1476.38, -5854.7) * mm, "end": v(-1476.38, -6413.5) * mm});
            skLineSegment(sketch, "E194.trimOffspring", {"start": v(-1425.58, -5854.7) * mm, "end": v(-1425.58, -6413.5) * mm});
            skLineSegment(sketch, "E195.trimOffspring", {"start": v(-1425.58, -5854.7) * mm, "end": v(-866.78, -5854.7) * mm});
            skLineSegment(sketch, "E196.trimOffspring", {"start": v(-1476.38, -6464.3) * mm, "end": v(-1476.38, -6731) * mm});
            skLineSegment(sketch, "E197.trimOffspring", {"start": v(-1425.58, -6464.3) * mm, "end": v(-866.78, -6464.3) * mm});
            skLineSegment(sketch, "E198.trimOffspring", {"start": v(-1425.58, -6464.3) * mm, "end": v(-1425.58, -6731) * mm});
            skLineSegment(sketch, "E199.trimOffspring", {"start": v(-1425.58, -6413.5) * mm, "end": v(-866.78, -6413.5) * mm});
            skLineSegment(sketch, "E200.trimOffspring", {"start": v(-815.98, -5194.3) * mm, "end": v(-257.18, -5194.3) * mm});
            skLineSegment(sketch, "E201.trimOffspring", {"start": v(-866.78, -5245.1) * mm, "end": v(-866.78, -5803.9) * mm});
            skLineSegment(sketch, "E202.trimOffspring", {"start": v(-815.98, -5245.1) * mm, "end": v(-815.98, -5803.9) * mm});
            skLineSegment(sketch, "E203.trimOffspring", {"start": v(-815.98, -5245.1) * mm, "end": v(-257.18, -5245.1) * mm});
            skLineSegment(sketch, "E204.trimOffspring", {"start": v(-815.98, -5803.9) * mm, "end": v(-257.17, -5803.9) * mm});
            skLineSegment(sketch, "E205.trimOffspring", {"start": v(-866.78, -5854.7) * mm, "end": v(-866.78, -6413.5) * mm});
            skLineSegment(sketch, "E206.trimOffspring", {"start": v(-815.98, -5854.7) * mm, "end": v(-257.17, -5854.7) * mm});
            skLineSegment(sketch, "E207.trimOffspring", {"start": v(-815.98, -5854.7) * mm, "end": v(-815.98, -6413.5) * mm});
            skLineSegment(sketch, "E208.trimOffspring", {"start": v(-815.98, -6413.5) * mm, "end": v(-257.18, -6413.5) * mm});
            skLineSegment(sketch, "E209.trimOffspring", {"start": v(-866.78, -6464.3) * mm, "end": v(-866.78, -6731) * mm});
            skLineSegment(sketch, "E210.trimOffspring", {"start": v(-815.98, -6464.3) * mm, "end": v(-257.18, -6464.3) * mm});
            skLineSegment(sketch, "E211.trimOffspring", {"start": v(-815.98, -6464.3) * mm, "end": v(-815.98, -6731) * mm});
            skLineSegment(sketch, "E212.trimOffspring", {"start": v(-206.37, -5194.3) * mm, "end": v(0, -5194.3) * mm});
            skLineSegment(sketch, "E213.trimOffspring", {"start": v(-257.18, -5245.1) * mm, "end": v(-257.18, -5803.9) * mm});
            skLineSegment(sketch, "E214.trimOffspring", {"start": v(-206.37, -5245.1) * mm, "end": v(0, -5245.1) * mm});
            skLineSegment(sketch, "E215.trimOffspring", {"start": v(-206.38, -5245.1) * mm, "end": v(-206.38, -5803.9) * mm});
            skLineSegment(sketch, "E216.trimOffspring", {"start": v(-206.37, -5803.9) * mm, "end": v(-34.92, -5803.9) * mm});
            skLineSegment(sketch, "E217.trimOffspring", {"start": v(-257.18, -5854.7) * mm, "end": v(-257.18, -6413.5) * mm});
            skLineSegment(sketch, "E218.trimOffspring", {"start": v(-206.38, -5854.7) * mm, "end": v(-206.38, -6413.5) * mm});
            skLineSegment(sketch, "E219.trimOffspring", {"start": v(-206.37, -5854.7) * mm, "end": v(-34.92, -5854.7) * mm});
            skLineSegment(sketch, "E220.trimOffspring", {"start": v(-206.37, -6413.5) * mm, "end": v(0, -6413.5) * mm});
            skLineSegment(sketch, "E221.trimOffspring", {"start": v(-257.18, -6464.3) * mm, "end": v(-257.18, -6731) * mm});
            skLineSegment(sketch, "E222.trimOffspring", {"start": v(-206.37, -6464.3) * mm, "end": v(0, -6464.3) * mm});
            skLineSegment(sketch, "E223.trimOffspring", {"start": v(-206.38, -6464.3) * mm, "end": v(-206.38, -6731) * mm});
            skSolve(sketch);
        }
        {
            var Q0;
            {var subQ0=sQuery(id+"F3.wireOp",EDGE,"E16.right");Q0=makeQuery(id+"F3.imprint","IMPRINT",FACE,{"disambiguationData":[TD([[makeQuery(id+"F3.imprint","IMPRINT",EDGE,{"derivedFrom":subQ0}),-1.0]])]});}
            var Q1;
            {var subQ0=sQuery(id+"F3.wireOp",EDGE,"E16.left");Q1=makeQuery(id+"F3.imprint","IMPRINT",FACE,{"disambiguationData":[TD([[makeQuery(id+"F3.imprint","IMPRINT",EDGE,{"derivedFrom":subQ0}),1.0]])]});}
            var Q2;
            {var subQ0=sQuery(id+"F3.wireOp",EDGE,"E17.left");Q2=makeQuery(id+"F3.imprint","IMPRINT",FACE,{"disambiguationData":[TD([[makeQuery(id+"F3.imprint","IMPRINT",EDGE,{"derivedFrom":subQ0}),1.0]])]});}
            var Q3;
            {var subQ0=sQuery(id+"F3.wireOp",EDGE,"E18.left");Q3=makeQuery(id+"F3.imprint","IMPRINT",FACE,{"disambiguationData":[TD([[makeQuery(id+"F3.imprint","IMPRINT",EDGE,{"derivedFrom":subQ0}),1.0]])]});}
            var Q4;
            {var subQ0=sQuery(id+"F3.wireOp",EDGE,"E19.right");Q4=makeQuery(id+"F3.imprint","IMPRINT",FACE,{"disambiguationData":[TD([[makeQuery(id+"F3.imprint","IMPRINT",EDGE,{"derivedFrom":subQ0}),1.0]])]});}
            var Q5;
            Q5=makeQuery(id+"F3.imprint","IMPRINT",FACE,{"disambiguationData":[TD([[makeQuery(id+"F3.imprint","IMPRINT",EDGE,{"derivedFrom":sQuery(id+"F3.wireOp",EDGE,"E53.trimOffspring")}),1.0]])]});
            var Q6;
            Q6=makeQuery(id+"F3.imprint","IMPRINT",FACE,{"disambiguationData":[TD([[makeQuery(id+"F3.imprint","IMPRINT",EDGE,{"derivedFrom":sQuery(id+"F3.wireOp",EDGE,"E49.trimOffspring")}),-1.0]])]});
            var Q7;
            Q7=makeQuery(id+"F3.imprint","IMPRINT",FACE,{"disambiguationData":[TD([[makeQuery(id+"F3.imprint","IMPRINT",EDGE,{"derivedFrom":sQuery(id+"F3.wireOp",EDGE,"E45.trimOffspring")}),1.0]])]});
            var Q8;
            Q8=makeQuery(id+"F3.imprint","IMPRINT",FACE,{"disambiguationData":[TD([[makeQuery(id+"F3.imprint","IMPRINT",EDGE,{"derivedFrom":sQuery(id+"F3.wireOp",EDGE,"E41.trimOffspring")}),1.0]])]});
            var Q9;
            {var subQ0=sQuery(id+"F3.wireOp",EDGE,"E30.bottom");Q9=makeQuery(id+"F3.imprint","IMPRINT",FACE,{"disambiguationData":[TD([[makeQuery(id+"F3.imprint","IMPRINT",EDGE,{"derivedFrom":subQ0}),1.0]])]});}
            var Q10;
            {var subQ0=sQuery(id+"F3.wireOp",EDGE,"E29.bottom");Q10=makeQuery(id+"F3.imprint","IMPRINT",FACE,{"disambiguationData":[TD([[makeQuery(id+"F3.imprint","IMPRINT",EDGE,{"derivedFrom":subQ0}),1.0]])]});}
            var Q11;
            Q11=makeQuery(id+"F3.imprint","IMPRINT",FACE,{"disambiguationData":[TD([[makeQuery(id+"F3.imprint","IMPRINT",EDGE,{"derivedFrom":sQuery(id+"F3.wireOp",EDGE,"E66.trimOffspring")}),-1.0]])]});
            var Q12;
            Q12=makeQuery(id+"F3.imprint","IMPRINT",FACE,{"disambiguationData":[TD([[makeQuery(id+"F3.imprint","IMPRINT",EDGE,{"derivedFrom":sQuery(id+"F3.wireOp",EDGE,"E60.trimOffspring")}),-1.0]])]});
            var Q13;
            Q13=makeQuery(id+"F3.imprint","IMPRINT",FACE,{"disambiguationData":[TD([[makeQuery(id+"F3.imprint","IMPRINT",EDGE,{"derivedFrom":sQuery(id+"F3.wireOp",EDGE,"E58.trimOffspring")}),-1.0]])]});
            var Q14;
            {var subQ0=sQuery(id+"F3.wireOp",EDGE,"E56.trimOffspring");Q14=makeQuery(id+"F3.imprint","IMPRINT",FACE,{"disambiguationData":[TD([[makeQuery(id+"F3.imprint","IMPRINT",EDGE,{"derivedFrom":subQ0}),-1.0]])]});}
            var Q15;
            Q15=makeQuery(id+"F3.imprint","IMPRINT",FACE,{"disambiguationData":[TD([[makeQuery(id+"F3.imprint","IMPRINT",EDGE,{"derivedFrom":sQuery(id+"F3.wireOp",EDGE,"E85.trimOffspring")}),1.0]])]});
            var Q16;
            Q16=makeQuery(id+"F3.imprint","IMPRINT",FACE,{"disambiguationData":[TD([[makeQuery(id+"F3.imprint","IMPRINT",EDGE,{"derivedFrom":sQuery(id+"F3.wireOp",EDGE,"E81.trimOffspring")}),1.0]])]});
            var Q17;
            Q17=makeQuery(id+"F3.imprint","IMPRINT",FACE,{"disambiguationData":[TD([[makeQuery(id+"F3.imprint","IMPRINT",EDGE,{"derivedFrom":sQuery(id+"F3.wireOp",EDGE,"E77.trimOffspring")}),1.0]])]});
            var Q18;
            Q18=makeQuery(id+"F3.imprint","IMPRINT",FACE,{"disambiguationData":[TD([[makeQuery(id+"F3.imprint","IMPRINT",EDGE,{"derivedFrom":sQuery(id+"F3.wireOp",EDGE,"E73.trimOffspring")}),1.0]])]});
            var Q19;
            {var subQ0=sQuery(id+"F3.wireOp",EDGE,"E28.bottom");Q19=makeQuery(id+"F3.imprint","IMPRINT",FACE,{"disambiguationData":[TD([[makeQuery(id+"F3.imprint","IMPRINT",EDGE,{"derivedFrom":subQ0}),1.0]])]});}
            var Q20;
            {var subQ4=sQuery(id+"F3.wireOp",EDGE,"E28.top");Q20=makeQuery(id+"F3.imprint","IMPRINT",FACE,{"disambiguationData":[TD([[makeQuery(id+"F3.imprint","IMPRINT",EDGE,{"derivedFrom":subQ4}),-1.0]])]});}
            var Q21;
            Q21=makeQuery(id+"F3.imprint","IMPRINT",FACE,{"disambiguationData":[TD([[makeQuery(id+"F3.imprint","IMPRINT",EDGE,{"derivedFrom":sQuery(id+"F3.wireOp",EDGE,"E34.trimOffspring")}),1.0]])]});
            var Q22;
            {var subQ0=sQuery(id+"F3.wireOp",EDGE,"E95.trimOffspring");Q22=makeQuery(id+"F3.imprint","IMPRINT",FACE,{"disambiguationData":[TD([[makeQuery(id+"F3.imprint","IMPRINT",EDGE,{"derivedFrom":subQ0}),1.0]])]});}
            var Q23;
            {var subQ5=sQuery(id+"F3.wireOp",EDGE,"E94.trimOffspring");Q23=makeQuery(id+"F3.imprint","IMPRINT",FACE,{"disambiguationData":[TD([[makeQuery(id+"F3.imprint","IMPRINT",EDGE,{"derivedFrom":subQ5}),-1.0]])]});}
            var Q24;
            {var subQ5=sQuery(id+"F3.wireOp",EDGE,"E89.trimOffspring");Q24=makeQuery(id+"F3.imprint","IMPRINT",FACE,{"disambiguationData":[TD([[makeQuery(id+"F3.imprint","IMPRINT",EDGE,{"derivedFrom":subQ5}),-1.0]])]});}
            var Q25;
            {var subQ5=sQuery(id+"F3.wireOp",EDGE,"E117.trimOffspring");Q25=makeQuery(id+"F3.imprint","IMPRINT",FACE,{"disambiguationData":[TD([[makeQuery(id+"F3.imprint","IMPRINT",EDGE,{"derivedFrom":subQ5}),1.0]])]});}
            var Q26;
            {var subQ5=sQuery(id+"F3.wireOp",EDGE,"E121.trimOffspring");Q26=makeQuery(id+"F3.imprint","IMPRINT",FACE,{"disambiguationData":[TD([[makeQuery(id+"F3.imprint","IMPRINT",EDGE,{"derivedFrom":subQ5}),1.0]])]});}
            var Q27;
            {var subQ0=sQuery(id+"F3.wireOp",EDGE,"E37.trimOffspring");Q27=makeQuery(id+"F3.imprint","IMPRINT",FACE,{"disambiguationData":[TD([[makeQuery(id+"F3.imprint","IMPRINT",EDGE,{"derivedFrom":subQ0}),1.0]])]});}
            var Q28;
            {var subQ0=sQuery(id+"F3.wireOp",EDGE,"E33.trimOffspring");Q28=makeQuery(id+"F3.imprint","IMPRINT",FACE,{"disambiguationData":[TD([[makeQuery(id+"F3.imprint","IMPRINT",EDGE,{"derivedFrom":subQ0}),1.0]])]});}
            var Q29;
            {var subQ4=sQuery(id+"F3.wireOp",EDGE,"E32.trimOffspring");Q29=makeQuery(id+"F3.imprint","IMPRINT",FACE,{"disambiguationData":[TD([[makeQuery(id+"F3.imprint","IMPRINT",EDGE,{"derivedFrom":subQ4}),-1.0]])]});}
            var Q30;
            {var subQ0=sQuery(id+"F3.wireOp",EDGE,"E26.bottom");Q30=makeQuery(id+"F3.imprint","IMPRINT",FACE,{"disambiguationData":[TD([[makeQuery(id+"F3.imprint","IMPRINT",EDGE,{"derivedFrom":subQ0}),1.0]])]});}
            var Q31;
            {var subQ2=sQuery(id+"F3.wireOp",EDGE,"E25.bottom");Q31=makeQuery(id+"F3.imprint","IMPRINT",FACE,{"disambiguationData":[TD([[makeQuery(id+"F3.imprint","IMPRINT",EDGE,{"derivedFrom":subQ2}),1.0]])]});}
            var Q32;
            Q32=makeQuery(id+"F3.imprint","IMPRINT",FACE,{"disambiguationData":[TD([[makeQuery(id+"F3.imprint","IMPRINT",EDGE,{"derivedFrom":sQuery(id+"F3.wireOp",EDGE,"E106.trimOffspring")}),1.0]])]});
            var Q33;
            Q33=makeQuery(id+"F3.imprint","IMPRINT",FACE,{"disambiguationData":[TD([[makeQuery(id+"F3.imprint","IMPRINT",EDGE,{"derivedFrom":sQuery(id+"F3.wireOp",EDGE,"E110.trimOffspring")}),1.0]])]});
            var Q34;
            Q34=makeQuery(id+"F3.imprint","IMPRINT",FACE,{"disambiguationData":[TD([[makeQuery(id+"F3.imprint","IMPRINT",EDGE,{"derivedFrom":sQuery(id+"F3.wireOp",EDGE,"E114.trimOffspring")}),1.0]])]});
            var Q35;
            Q35=makeQuery(id+"F3.imprint","IMPRINT",FACE,{"disambiguationData":[TD([[makeQuery(id+"F3.imprint","IMPRINT",EDGE,{"derivedFrom":sQuery(id+"F3.wireOp",EDGE,"E118.trimOffspring")}),-1.0]])]});
            var Q36;
            Q36=makeQuery(id+"F3.imprint","IMPRINT",FACE,{"disambiguationData":[TD([[makeQuery(id+"F3.imprint","IMPRINT",EDGE,{"derivedFrom":sQuery(id+"F3.wireOp",EDGE,"E116.trimOffspring")}),1.0]])]});
            var Q37;
            {var subQ0=sQuery(id+"F3.wireOp",EDGE,"E24.bottom");Q37=makeQuery(id+"F3.imprint","IMPRINT",FACE,{"disambiguationData":[TD([[makeQuery(id+"F3.imprint","IMPRINT",EDGE,{"derivedFrom":subQ0}),1.0]])]});}
            var Q38;
            Q38=makeQuery(id+"F3.imprint","IMPRINT",FACE,{"disambiguationData":[TD([[makeQuery(id+"F3.imprint","IMPRINT",EDGE,{"derivedFrom":sQuery(id+"F3.wireOp",EDGE,"E139.trimOffspring")}),-1.0]])]});
            var Q39;
            Q39=makeQuery(id+"F3.imprint","IMPRINT",FACE,{"disambiguationData":[TD([[makeQuery(id+"F3.imprint","IMPRINT",EDGE,{"derivedFrom":sQuery(id+"F3.wireOp",EDGE,"E134.trimOffspring")}),-1.0]])]});
            var Q40;
            Q40=makeQuery(id+"F3.imprint","IMPRINT",FACE,{"disambiguationData":[TD([[makeQuery(id+"F3.imprint","IMPRINT",EDGE,{"derivedFrom":sQuery(id+"F3.wireOp",EDGE,"E130.trimOffspring")}),-1.0]])]});
            var Q41;
            Q41=makeQuery(id+"F3.imprint","IMPRINT",FACE,{"disambiguationData":[TD([[makeQuery(id+"F3.imprint","IMPRINT",EDGE,{"derivedFrom":sQuery(id+"F3.wireOp",EDGE,"E127.trimOffspring")}),-1.0]])]});
            var Q42;
            Q42=makeQuery(id+"F3.imprint","IMPRINT",FACE,{"disambiguationData":[TD([[makeQuery(id+"F3.imprint","IMPRINT",EDGE,{"derivedFrom":sQuery(id+"F3.wireOp",EDGE,"E124.trimOffspring")}),1.0]])]});
            var Q43;
            Q43=makeQuery(id+"F3.imprint","IMPRINT",FACE,{"disambiguationData":[TD([[makeQuery(id+"F3.imprint","IMPRINT",EDGE,{"derivedFrom":sQuery(id+"F3.wireOp",EDGE,"E162.trimOffspring")}),1.0]])]});
            var Q44;
            Q44=makeQuery(id+"F3.imprint","IMPRINT",FACE,{"disambiguationData":[TD([[makeQuery(id+"F3.imprint","IMPRINT",EDGE,{"derivedFrom":sQuery(id+"F3.wireOp",EDGE,"E158.trimOffspring")}),-1.0]])]});
            var Q45;
            Q45=makeQuery(id+"F3.imprint","IMPRINT",FACE,{"disambiguationData":[TD([[makeQuery(id+"F3.imprint","IMPRINT",EDGE,{"derivedFrom":sQuery(id+"F3.wireOp",EDGE,"E154.trimOffspring")}),1.0]])]});
            var Q46;
            Q46=makeQuery(id+"F3.imprint","IMPRINT",FACE,{"disambiguationData":[TD([[makeQuery(id+"F3.imprint","IMPRINT",EDGE,{"derivedFrom":sQuery(id+"F3.wireOp",EDGE,"E150.trimOffspring")}),1.0]])]});
            var Q47;
            Q47=makeQuery(id+"F3.imprint","IMPRINT",FACE,{"disambiguationData":[TD([[makeQuery(id+"F3.imprint","IMPRINT",EDGE,{"derivedFrom":sQuery(id+"F3.wireOp",EDGE,"E146.trimOffspring")}),1.0]])]});
            var Q48;
            {var subQ0=sQuery(id+"F3.wireOp",EDGE,"E23.top");Q48=makeQuery(id+"F3.imprint","IMPRINT",FACE,{"disambiguationData":[TD([[makeQuery(id+"F3.imprint","IMPRINT",EDGE,{"derivedFrom":subQ0}),1.0]])]});}
            var Q49;
            {var subQ0=sQuery(id+"F3.wireOp",EDGE,"E22.top");Q49=makeQuery(id+"F3.imprint","IMPRINT",FACE,{"disambiguationData":[TD([[makeQuery(id+"F3.imprint","IMPRINT",EDGE,{"derivedFrom":subQ0}),1.0]])]});}
            var Q50;
            Q50=makeQuery(id+"F3.imprint","IMPRINT",FACE,{"disambiguationData":[TD([[makeQuery(id+"F3.imprint","IMPRINT",EDGE,{"derivedFrom":sQuery(id+"F3.wireOp",EDGE,"E166.trimOffspring")}),-1.0]])]});
            var Q51;
            Q51=makeQuery(id+"F3.imprint","IMPRINT",FACE,{"disambiguationData":[TD([[makeQuery(id+"F3.imprint","IMPRINT",EDGE,{"derivedFrom":sQuery(id+"F3.wireOp",EDGE,"E178.trimOffspring")}),1.0]])]});
            var Q52;
            Q52=makeQuery(id+"F3.imprint","IMPRINT",FACE,{"disambiguationData":[TD([[makeQuery(id+"F3.imprint","IMPRINT",EDGE,{"derivedFrom":sQuery(id+"F3.wireOp",EDGE,"E190.trimOffspring")}),1.0]])]});
            var Q53;
            Q53=makeQuery(id+"F3.imprint","IMPRINT",FACE,{"disambiguationData":[TD([[makeQuery(id+"F3.imprint","IMPRINT",EDGE,{"derivedFrom":sQuery(id+"F3.wireOp",EDGE,"E202.trimOffspring")}),1.0]])]});
            var Q54;
            {var subQ0=sQuery(id+"F3.wireOp",EDGE,"E215.trimOffspring");Q54=makeQuery(id+"F3.imprint","IMPRINT",FACE,{"disambiguationData":[TD([[makeQuery(id+"F3.imprint","IMPRINT",EDGE,{"derivedFrom":subQ0}),1.0]])]});}
            var Q55;
            Q55=makeQuery(id+"F3.imprint","IMPRINT",FACE,{"disambiguationData":[TD([[makeQuery(id+"F3.imprint","IMPRINT",EDGE,{"derivedFrom":sQuery(id+"F3.wireOp",EDGE,"E218.trimOffspring")}),1.0]])]});
            var Q56;
            Q56=makeQuery(id+"F3.imprint","IMPRINT",FACE,{"disambiguationData":[TD([[makeQuery(id+"F3.imprint","IMPRINT",EDGE,{"derivedFrom":sQuery(id+"F3.wireOp",EDGE,"E206.trimOffspring")}),-1.0]])]});
            var Q57;
            Q57=makeQuery(id+"F3.imprint","IMPRINT",FACE,{"disambiguationData":[TD([[makeQuery(id+"F3.imprint","IMPRINT",EDGE,{"derivedFrom":sQuery(id+"F3.wireOp",EDGE,"E194.trimOffspring")}),1.0]])]});
            var Q58;
            Q58=makeQuery(id+"F3.imprint","IMPRINT",FACE,{"disambiguationData":[TD([[makeQuery(id+"F3.imprint","IMPRINT",EDGE,{"derivedFrom":sQuery(id+"F3.wireOp",EDGE,"E182.trimOffspring")}),1.0]])]});
            var Q59;
            Q59=makeQuery(id+"F3.imprint","IMPRINT",FACE,{"disambiguationData":[TD([[makeQuery(id+"F3.imprint","IMPRINT",EDGE,{"derivedFrom":sQuery(id+"F3.wireOp",EDGE,"E170.trimOffspring")}),-1.0]])]});
            var Q60;
            {var subQ0=sQuery(id+"F3.wireOp",EDGE,"E21.bottom");Q60=makeQuery(id+"F3.imprint","IMPRINT",FACE,{"disambiguationData":[TD([[makeQuery(id+"F3.imprint","IMPRINT",EDGE,{"derivedFrom":subQ0}),1.0]])]});}
            var Q61;
            {var subQ0=sQuery(id+"F3.wireOp",EDGE,"E21.top");Q61=makeQuery(id+"F3.imprint","IMPRINT",FACE,{"disambiguationData":[TD([[makeQuery(id+"F3.imprint","IMPRINT",EDGE,{"derivedFrom":subQ0}),-1.0]])]});}
            var Q62;
            Q62=makeQuery(id+"F3.imprint","IMPRINT",FACE,{"disambiguationData":[TD([[makeQuery(id+"F3.imprint","IMPRINT",EDGE,{"derivedFrom":sQuery(id+"F3.wireOp",EDGE,"E174.trimOffspring")}),-1.0]])]});
            var Q63;
            Q63=makeQuery(id+"F3.imprint","IMPRINT",FACE,{"disambiguationData":[TD([[makeQuery(id+"F3.imprint","IMPRINT",EDGE,{"derivedFrom":sQuery(id+"F3.wireOp",EDGE,"E186.trimOffspring")}),-1.0]])]});
            var Q64;
            Q64=makeQuery(id+"F3.imprint","IMPRINT",FACE,{"disambiguationData":[TD([[makeQuery(id+"F3.imprint","IMPRINT",EDGE,{"derivedFrom":sQuery(id+"F3.wireOp",EDGE,"E197.trimOffspring")}),-1.0]])]});
            var Q65;
            Q65=makeQuery(id+"F3.imprint","IMPRINT",FACE,{"disambiguationData":[TD([[makeQuery(id+"F3.imprint","IMPRINT",EDGE,{"derivedFrom":sQuery(id+"F3.wireOp",EDGE,"E210.trimOffspring")}),-1.0]])]});
            var Q66;
            {var subQ0=sQuery(id+"F3.wireOp",EDGE,"E222.trimOffspring");Q66=makeQuery(id+"F3.imprint","IMPRINT",FACE,{"disambiguationData":[TD([[makeQuery(id+"F3.imprint","IMPRINT",EDGE,{"derivedFrom":subQ0}),-1.0]])]});}
            extrude(context, id + "F4", {"entities" : qUnion([Q0, Q1, Q2, Q3, Q4, Q5, Q6, Q7, Q8, Q9, Q10, Q11, Q12, Q13, Q14, Q15, Q16, Q17, Q18, Q19, Q20, Q21, Q22, Q23, Q24, Q25, Q26, Q27, Q28, Q29, Q30, Q31, Q32, Q33, Q34, Q35, Q36, Q37, Q38, Q39, Q40, Q41, Q42, Q43, Q44, Q45, Q46, Q47, Q48, Q49, Q50, Q51, Q52, Q53, Q54, Q55, Q56, Q57, Q58, Q59, Q60, Q61, Q62, Q63, Q64, Q65, Q66]), "operationType" : NewBodyOperationType.REMOVE, "oppositeDirection" : true, "depth" : 50.8 * mm, "offsetDistance" : 25.4 * mm});
        }
    });
